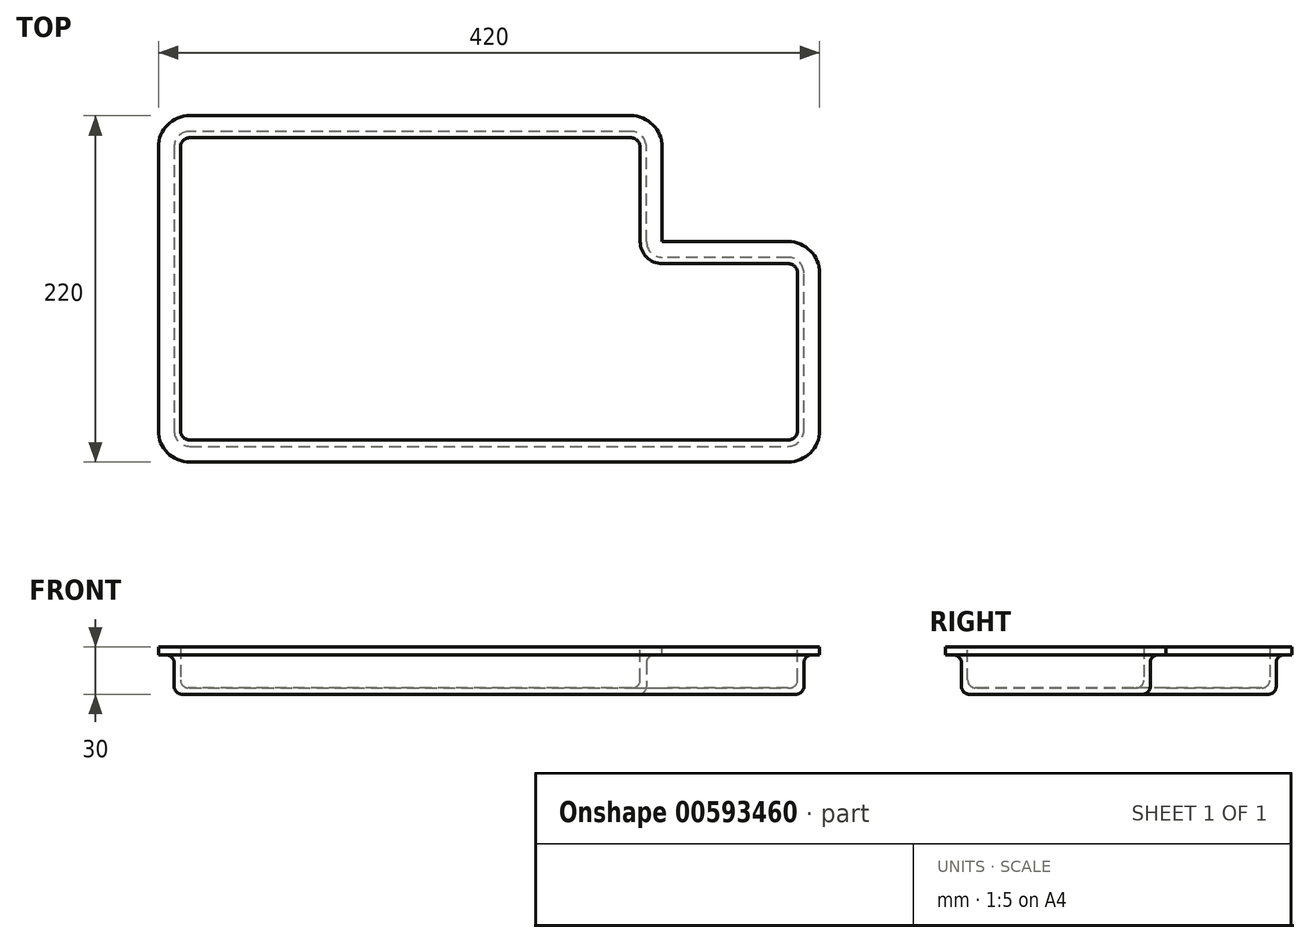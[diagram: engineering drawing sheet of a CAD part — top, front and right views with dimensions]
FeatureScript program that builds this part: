
annotation { "Feature Type Name" : "Feature", "Feature Type Description" : "" }
export const myFeature = defineFeature(function(context is Context, id is Id, definition is map)
    precondition{}
    {
        {
            var Q0;
            Q0=qCreatedBy(makeId("Top.planeOp"),FACE);
            var sketch = newSketch(context, id + "F0", { "sketchPlane" : qUnion([Q0])});
            skLineSegment(sketch, "E0", {"start": v(-93.08, 130.1) * mm, "end": v(-93.08, -49.9) * mm});
            skLineSegment(sketch, "E1", {"start": v(-83.08, -59.9) * mm, "end": v(296.92, -59.9) * mm});
            skLineSegment(sketch, "E2", {"start": v(306.92, -49.9) * mm, "end": v(306.92, 50.1) * mm});
            skLineSegment(sketch, "E3", {"start": v(296.92, 60.1) * mm, "end": v(216.92, 60.1) * mm});
            skLineSegment(sketch, "E4", {"start": v(206.92, 70.1) * mm, "end": v(206.92, 130.1) * mm});
            skLineSegment(sketch, "E5", {"start": v(196.92, 140.1) * mm, "end": v(-83.08, 140.1) * mm});
            skPoint(sketch, "E6.visualSharp", {"position": v(-93.08, 140.1) * mm});
            skArc(sketch, "E6.filletArc", {"start": v(-83.08, 140.1) * mm, "mid": v(-90.16, 137.17) * mm, "end": v(-93.08, 130.1) * mm});
            skPoint(sketch, "E7.visualSharp", {"position": v(206.92, 140.1) * mm});
            skArc(sketch, "E7.filletArc", {"start": v(206.92, 130.1) * mm, "mid": v(203.99, 137.17) * mm, "end": v(196.92, 140.1) * mm});
            skPoint(sketch, "E8.visualSharp", {"position": v(306.92, 60.1) * mm});
            skArc(sketch, "E8.filletArc", {"start": v(306.92, 50.1) * mm, "mid": v(303.99, 57.17) * mm, "end": v(296.92, 60.1) * mm});
            skPoint(sketch, "E9.visualSharp", {"position": v(206.92, 60.1) * mm});
            skArc(sketch, "E9.filletArc", {"start": v(206.92, 70.1) * mm, "mid": v(209.84, 63.03) * mm, "end": v(216.92, 60.1) * mm});
            skPoint(sketch, "E10.visualSharp", {"position": v(306.92, -59.9) * mm});
            skArc(sketch, "E10.filletArc", {"start": v(296.92, -59.9) * mm, "mid": v(303.99, -56.97) * mm, "end": v(306.92, -49.9) * mm});
            skPoint(sketch, "E11.visualSharp", {"position": v(-93.08, -59.9) * mm});
            skArc(sketch, "E11.filletArc", {"start": v(-93.08, -49.9) * mm, "mid": v(-90.16, -56.97) * mm, "end": v(-83.08, -59.9) * mm});
            skSolve(sketch);
        }
        {
            var Q0;
            Q0=makeQuery(id+"F0.imprint","IMPRINT",FACE,{"disambiguationData":[TD([[makeQuery(id+"F0.imprint","IMPRINT",EDGE,{"derivedFrom":sQuery(id+"F0.wireOp",EDGE,"E0")}),1.0]])]});
            extrude(context, id + "F1", {"entities" : qUnion([Q0]), "depth" : 30 * mm, "offsetDistance" : 25 * mm});
        }
        {
            var Q0;
            Q0=makeQuery(id+"F1.opExtrude","CAP_FACE",FACE,{"disambiguationData":[OSD([sQuery(id+"F0.wireOp",EDGE,"E0"),sQuery(id+"F0.wireOp",EDGE,"E1"),sQuery(id+"F0.wireOp",EDGE,"E2"),sQuery(id+"F0.wireOp",EDGE,"E3"),sQuery(id+"F0.wireOp",EDGE,"E4"),sQuery(id+"F0.wireOp",EDGE,"E5"),sQuery(id+"F0.wireOp",EDGE,"E6.filletArc"),sQuery(id+"F0.wireOp",EDGE,"E7.filletArc"),sQuery(id+"F0.wireOp",EDGE,"E8.filletArc"),sQuery(id+"F0.wireOp",EDGE,"E9.filletArc"),sQuery(id+"F0.wireOp",EDGE,"E10.filletArc"),sQuery(id+"F0.wireOp",EDGE,"E11.filletArc")])],"isStart":false});
            shell(context, id + "F2", {"entities" : qUnion([Q0]), "thickness" : 4 * mm});
        }
        {
            var Q0;
            Q0=makeQuery(id+"F1.opExtrude","CAP_FACE",FACE,{"disambiguationData":[OSD([sQuery(id+"F0.wireOp",EDGE,"E0"),sQuery(id+"F0.wireOp",EDGE,"E1"),sQuery(id+"F0.wireOp",EDGE,"E2"),sQuery(id+"F0.wireOp",EDGE,"E3"),sQuery(id+"F0.wireOp",EDGE,"E4"),sQuery(id+"F0.wireOp",EDGE,"E5"),sQuery(id+"F0.wireOp",EDGE,"E6.filletArc"),sQuery(id+"F0.wireOp",EDGE,"E7.filletArc"),sQuery(id+"F0.wireOp",EDGE,"E8.filletArc"),sQuery(id+"F0.wireOp",EDGE,"E9.filletArc"),sQuery(id+"F0.wireOp",EDGE,"E10.filletArc"),sQuery(id+"F0.wireOp",EDGE,"E11.filletArc")])],"isStart":false});
            var sketch = newSketch(context, id + "F3", { "sketchPlane" : qUnion([Q0])});
            skArc(sketch, "E12.0", {"start": v(-83.08, 150.1) * mm, "mid": v(-97.23, 144.24) * mm, "end": v(-103.08, 130.1) * mm});
            skLineSegment(sketch, "E12.1", {"start": v(196.92, 150.1) * mm, "end": v(-83.08, 150.1) * mm});
            skArc(sketch, "E12.2", {"start": v(216.92, 130.1) * mm, "mid": v(211.06, 144.24) * mm, "end": v(196.92, 150.1) * mm});
            skArc(sketch, "E12.3", {"start": v(316.92, 50.1) * mm, "mid": v(311.06, 64.24) * mm, "end": v(296.92, 70.1) * mm});
            skLineSegment(sketch, "E12.4", {"start": v(296.92, 70.1) * mm, "end": v(216.92, 70.1) * mm});
            skLineSegment(sketch, "E12.5", {"start": v(216.92, 70.1) * mm, "end": v(216.92, 70.1) * mm});
            skLineSegment(sketch, "E12.6", {"start": v(216.92, 70.1) * mm, "end": v(216.92, 130.1) * mm});
            skLineSegment(sketch, "E13.0", {"start": v(316.92, -49.9) * mm, "end": v(316.92, 50.1) * mm});
            skLineSegment(sketch, "E13.1", {"start": v(-103.08, 130.1) * mm, "end": v(-103.08, -49.9) * mm});
            skArc(sketch, "E13.2", {"start": v(-103.08, -49.9) * mm, "mid": v(-97.23, -64.04) * mm, "end": v(-83.08, -69.9) * mm});
            skLineSegment(sketch, "E13.3", {"start": v(-83.08, -69.9) * mm, "end": v(296.92, -69.9) * mm});
            skArc(sketch, "E13.4", {"start": v(296.92, -69.9) * mm, "mid": v(311.06, -64.04) * mm, "end": v(316.92, -49.9) * mm});
            skArc(sketch, "E14.0", {"start": v(202.92, 130.1) * mm, "mid": v(201.16, 134.34) * mm, "end": v(196.92, 136.1) * mm});
            skLineSegment(sketch, "E14.1", {"start": v(-83.08, -55.9) * mm, "end": v(296.92, -55.9) * mm});
            skArc(sketch, "E14.2", {"start": v(-89.08, -49.9) * mm, "mid": v(-87.33, -54.14) * mm, "end": v(-83.08, -55.9) * mm});
            skLineSegment(sketch, "E14.3", {"start": v(-89.08, 130.1) * mm, "end": v(-89.08, -49.9) * mm});
            skArc(sketch, "E14.4", {"start": v(-83.08, 136.1) * mm, "mid": v(-87.33, 134.34) * mm, "end": v(-89.08, 130.1) * mm});
            skArc(sketch, "E14.5", {"start": v(296.92, -55.9) * mm, "mid": v(301.16, -54.14) * mm, "end": v(302.92, -49.9) * mm});
            skLineSegment(sketch, "E14.6", {"start": v(196.92, 136.1) * mm, "end": v(-83.08, 136.1) * mm});
            skLineSegment(sketch, "E14.7", {"start": v(302.92, -49.9) * mm, "end": v(302.92, 50.1) * mm});
            skArc(sketch, "E14.8", {"start": v(302.92, 50.1) * mm, "mid": v(301.16, 54.34) * mm, "end": v(296.92, 56.1) * mm});
            skLineSegment(sketch, "E14.9", {"start": v(296.92, 56.1) * mm, "end": v(216.92, 56.1) * mm});
            skArc(sketch, "E14.10", {"start": v(202.92, 70.1) * mm, "mid": v(207.02, 60.2) * mm, "end": v(216.92, 56.1) * mm});
            skLineSegment(sketch, "E14.11", {"start": v(202.92, 70.1) * mm, "end": v(202.92, 130.1) * mm});
            skSolve(sketch);
        }
        {
            var Q0;
            Q0 = qSketchRegion(id + "F3", true);
            extrude(context, id + "F4", {"entities" : qUnion([Q0]), "operationType" : NewBodyOperationType.ADD, "oppositeDirection" : true, "depth" : 5 * mm, "offsetDistance" : 25 * mm});
        }
        {
            var Q0;
            Q0=makeQuery(id+"F2.opShell","OFFSET_FACE",FACE,{"disambiguationData":[OSD([sQuery(id+"F0.wireOp",EDGE,"E0"),sQuery(id+"F0.wireOp",EDGE,"E1"),sQuery(id+"F0.wireOp",EDGE,"E2"),sQuery(id+"F0.wireOp",EDGE,"E3"),sQuery(id+"F0.wireOp",EDGE,"E4"),sQuery(id+"F0.wireOp",EDGE,"E5"),sQuery(id+"F0.wireOp",EDGE,"E6.filletArc"),sQuery(id+"F0.wireOp",EDGE,"E7.filletArc"),sQuery(id+"F0.wireOp",EDGE,"E8.filletArc"),sQuery(id+"F0.wireOp",EDGE,"E9.filletArc"),sQuery(id+"F0.wireOp",EDGE,"E10.filletArc"),sQuery(id+"F0.wireOp",EDGE,"E11.filletArc")])]});
            fillet(context, id + "F5", {"entities" : qUnion([Q0]), "radius" : 5 * mm, "tangentPropagation" : true, "allowEdgeOverflow" : false});
        }
        {
            var Q0;
            Q0=makeQuery(id+"F4.boolean.opBoolean","INTERSECT",EDGE,{"derivedFrom":[makeQuery(id+"F1.opExtrude","SWEPT_FACE",FACE,{"disambiguationData":[OSD([sQuery(id+"F0.wireOp",EDGE,"E1")])]}),makeQuery(id+"F4.opExtrude","CAP_FACE",FACE,{"disambiguationData":[OSD([sQuery(id+"F3.wireOp",EDGE,"E12.0"),sQuery(id+"F3.wireOp",EDGE,"E12.1"),sQuery(id+"F3.wireOp",EDGE,"E12.2"),sQuery(id+"F3.wireOp",EDGE,"E12.3"),sQuery(id+"F3.wireOp",EDGE,"E12.4"),sQuery(id+"F3.wireOp",EDGE,"E12.6"),sQuery(id+"F3.wireOp",EDGE,"E13.0"),sQuery(id+"F3.wireOp",EDGE,"E13.1"),sQuery(id+"F3.wireOp",EDGE,"E13.2"),sQuery(id+"F3.wireOp",EDGE,"E13.3"),sQuery(id+"F3.wireOp",EDGE,"E13.4"),sQuery(id+"F3.wireOp",EDGE,"E14.0"),sQuery(id+"F3.wireOp",EDGE,"E14.1"),sQuery(id+"F3.wireOp",EDGE,"E14.2"),sQuery(id+"F3.wireOp",EDGE,"E14.3"),sQuery(id+"F3.wireOp",EDGE,"E14.4"),sQuery(id+"F3.wireOp",EDGE,"E14.5"),sQuery(id+"F3.wireOp",EDGE,"E14.6"),sQuery(id+"F3.wireOp",EDGE,"E14.7"),sQuery(id+"F3.wireOp",EDGE,"E14.8"),sQuery(id+"F3.wireOp",EDGE,"E14.9"),sQuery(id+"F3.wireOp",EDGE,"E14.10"),sQuery(id+"F3.wireOp",EDGE,"E14.11")])],"isStart":false})]});
            var Q1;
            Q1=makeQuery(id+"F1.opExtrude","CAP_EDGE",EDGE,{"disambiguationData":[OSD([sQuery(id+"F0.wireOp",EDGE,"E1")])],"isStart":true});
            fillet(context, id + "F6", {"entities" : qUnion([Q0, Q1]), "radius" : 5 * mm, "tangentPropagation" : true, "allowEdgeOverflow" : false});
        }
    });
